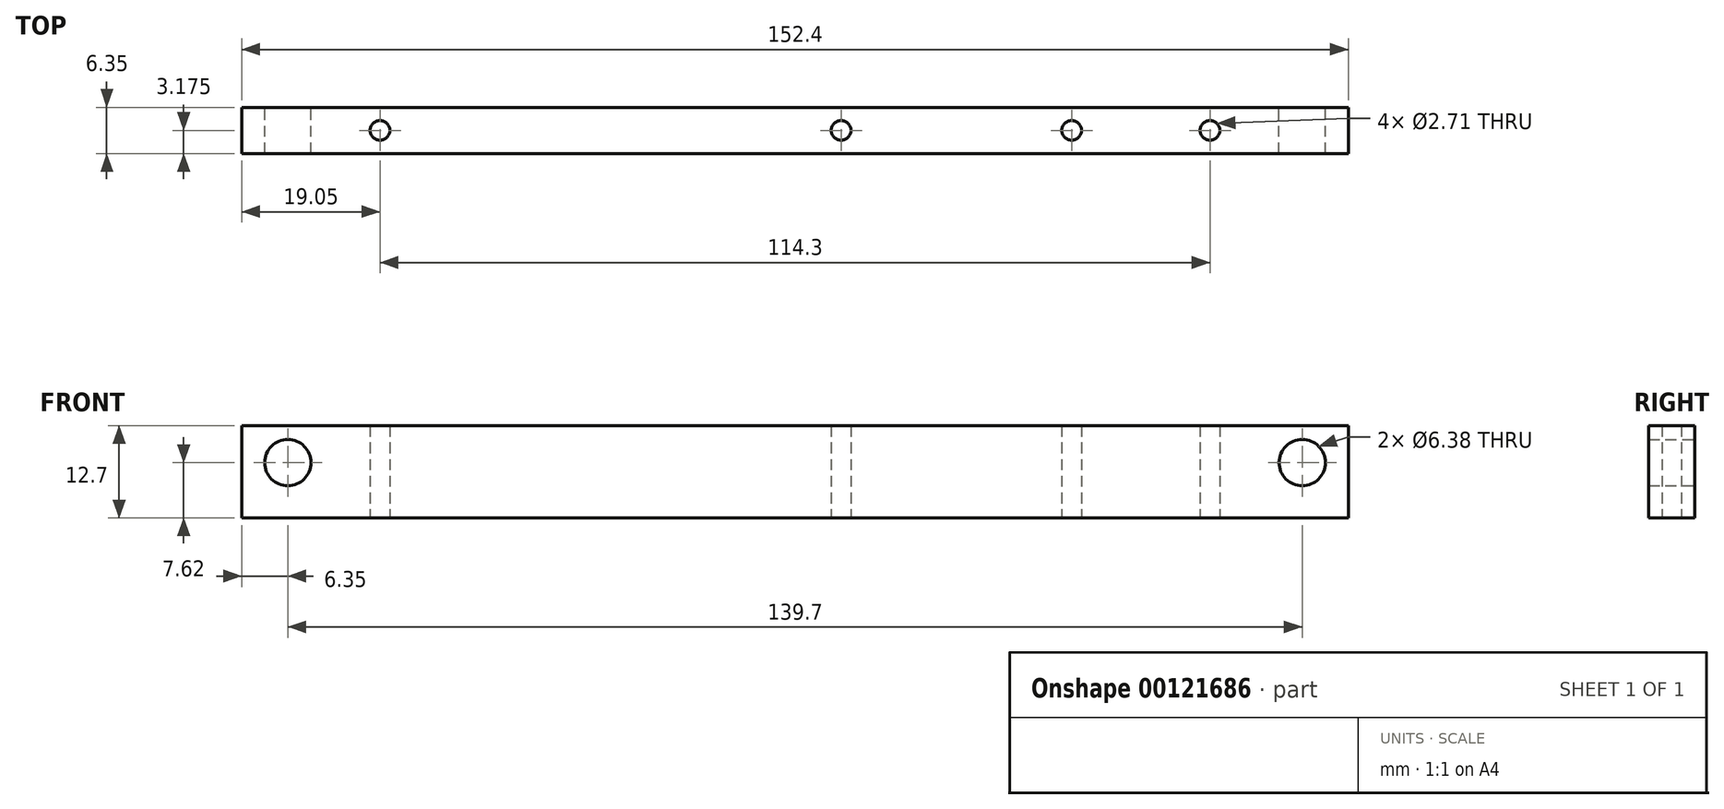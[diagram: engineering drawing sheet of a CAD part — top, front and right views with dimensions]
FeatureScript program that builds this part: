
annotation { "Feature Type Name" : "Feature", "Feature Type Description" : "" }
export const myFeature = defineFeature(function(context is Context, id is Id, definition is map)
    precondition{}
    {
        {
            var Q0;
            Q0=qCreatedBy(makeId("Front.planeOp"),FACE);
            var sketch = newSketch(context, id + "F0", { "sketchPlane" : qUnion([Q0])});
            skLineSegment(sketch, "E0.bottom", {"start": v(76.2, -6.35) * mm, "end": v(-76.2, -6.35) * mm});
            skLineSegment(sketch, "E0.top", {"start": v(76.2, 6.35) * mm, "end": v(-76.2, 6.35) * mm});
            skLineSegment(sketch, "E0.left", {"start": v(76.2, -6.35) * mm, "end": v(76.2, 6.35) * mm});
            skLineSegment(sketch, "E0.right", {"start": v(-76.2, -6.35) * mm, "end": v(-76.2, 6.35) * mm});
            skPoint(sketch, "E0.middle", {"position": v(0, 0) * mm});
            skCircle(sketch, "E1", {"center": v(-69.85, 1.27) * mm, "radius": 3.19 * mm});
            skCircle(sketch, "E2", {"center": v(69.85, 1.27) * mm, "radius": 3.19 * mm});
            skSolve(sketch);
        }
        {
            var Q0;
            Q0 = qSketchRegion(id + "F0", true);
            extrude(context, id + "F1", {"entities" : qUnion([Q0]), "depth" : 6.35 * mm});
        }
        {
            var Q0;
            Q0=makeQuery(id+"F1.opExtrude","SWEPT_FACE",FACE,{"disambiguationData":[OSD([sQuery(id+"F0.wireOp",EDGE,"E0.bottom")])]});
            var sketch = newSketch(context, id + "F2", { "sketchPlane" : qUnion([Q0])});
            skCircle(sketch, "E3", {"center": v(-57.15, 3.17) * mm, "radius": 1.83 * mm});
            skCircle(sketch, "E4", {"center": v(57.15, 3.18) * mm, "radius": 1.83 * mm});
            skCircle(sketch, "E5", {"center": v(6.35, 3.17) * mm, "radius": 1.83 * mm});
            skCircle(sketch, "E6", {"center": v(38.1, 3.18) * mm, "radius": 1.83 * mm});
            skSolve(sketch);
        }
        {
            var Q0;
            Q0=sQuery(id+"F2.wireOp",VERTEX,"E3.center");
            var Q1;
            Q1=sQuery(id+"F2.wireOp",VERTEX,"E4.center");
            var Q2;
            Q2=makeQuery(id+"F1.opExtrude","SWEPT_BODY",BODY,{"disambiguationData":[OSD([sQuery(id+"F0.wireOp",EDGE,"E0.bottom"),sQuery(id+"F0.wireOp",EDGE,"E0.top"),sQuery(id+"F0.wireOp",EDGE,"E0.left"),sQuery(id+"F0.wireOp",EDGE,"E0.right"),sQuery(id+"F0.wireOp",EDGE,"E1"),sQuery(id+"F0.wireOp",EDGE,"E2")])]});
            hole(context, id + "F3", {"style" : HoleStyle.SIMPLE, "endStyle" : HoleEndStyle.THROUGH, "standardTappedOrClearance" : lookupTablePath({ "standard" : "ANSI", "engagement" : "75%", "pitch" : "32 tpi", "size" : "#6", "type" : "Tapped" }), "standardBlindInLast" : lookupTablePath({ "standard" : "ANSI", "engagement" : "75%", "pitch" : "32 tpi", "size" : "#6", "type" : "Tapped" }), "holeDiameter" : 2.7 * mm, "locations" : qUnion([Q0, Q1]), "scope" : qUnion([Q2]), "isTappedThrough" : true, "majorDiameter" : 3.5 * mm, "showTappedDepth" : true});
        }
        {
            var Q0;
            Q0=sQuery(id+"F2.wireOp",VERTEX,"E5.center");
            var Q1;
            Q1=makeQuery(id+"F1.opExtrude","SWEPT_BODY",BODY,{"disambiguationData":[OSD([sQuery(id+"F0.wireOp",EDGE,"E0.bottom"),sQuery(id+"F0.wireOp",EDGE,"E0.top"),sQuery(id+"F0.wireOp",EDGE,"E0.left"),sQuery(id+"F0.wireOp",EDGE,"E0.right"),sQuery(id+"F0.wireOp",EDGE,"E1"),sQuery(id+"F0.wireOp",EDGE,"E2")])]});
            hole(context, id + "F4", {"style" : HoleStyle.SIMPLE, "endStyle" : HoleEndStyle.THROUGH, "standardTappedOrClearance" : lookupTablePath({ "standard" : "ANSI", "engagement" : "75%", "pitch" : "32 tpi", "size" : "#6", "type" : "Tapped" }), "standardBlindInLast" : lookupTablePath({ "standard" : "ANSI", "engagement" : "75%", "pitch" : "32 tpi", "size" : "#6", "type" : "Tapped" }), "holeDiameter" : 2.7 * mm, "locations" : qUnion([Q0]), "scope" : qUnion([Q1]), "isTappedThrough" : true, "majorDiameter" : 3.5 * mm, "showTappedDepth" : true});
        }
        {
            var Q0;
            Q0=sQuery(id+"F2.wireOp",VERTEX,"E6.center");
            var Q1;
            Q1=makeQuery(id+"F1.opExtrude","SWEPT_BODY",BODY,{"disambiguationData":[OSD([sQuery(id+"F0.wireOp",EDGE,"E0.bottom"),sQuery(id+"F0.wireOp",EDGE,"E0.top"),sQuery(id+"F0.wireOp",EDGE,"E0.left"),sQuery(id+"F0.wireOp",EDGE,"E0.right"),sQuery(id+"F0.wireOp",EDGE,"E1"),sQuery(id+"F0.wireOp",EDGE,"E2")])]});
            hole(context, id + "F5", {"style" : HoleStyle.SIMPLE, "endStyle" : HoleEndStyle.THROUGH, "standardTappedOrClearance" : lookupTablePath({ "standard" : "ANSI", "engagement" : "75%", "pitch" : "32 tpi", "size" : "#6", "type" : "Tapped" }), "standardBlindInLast" : lookupTablePath({ "standard" : "ANSI", "engagement" : "75%", "pitch" : "32 tpi", "size" : "#6", "type" : "Tapped" }), "holeDiameter" : 2.7 * mm, "locations" : qUnion([Q0]), "scope" : qUnion([Q1]), "isTappedThrough" : true, "majorDiameter" : 3.5 * mm, "showTappedDepth" : true});
        }
    });
